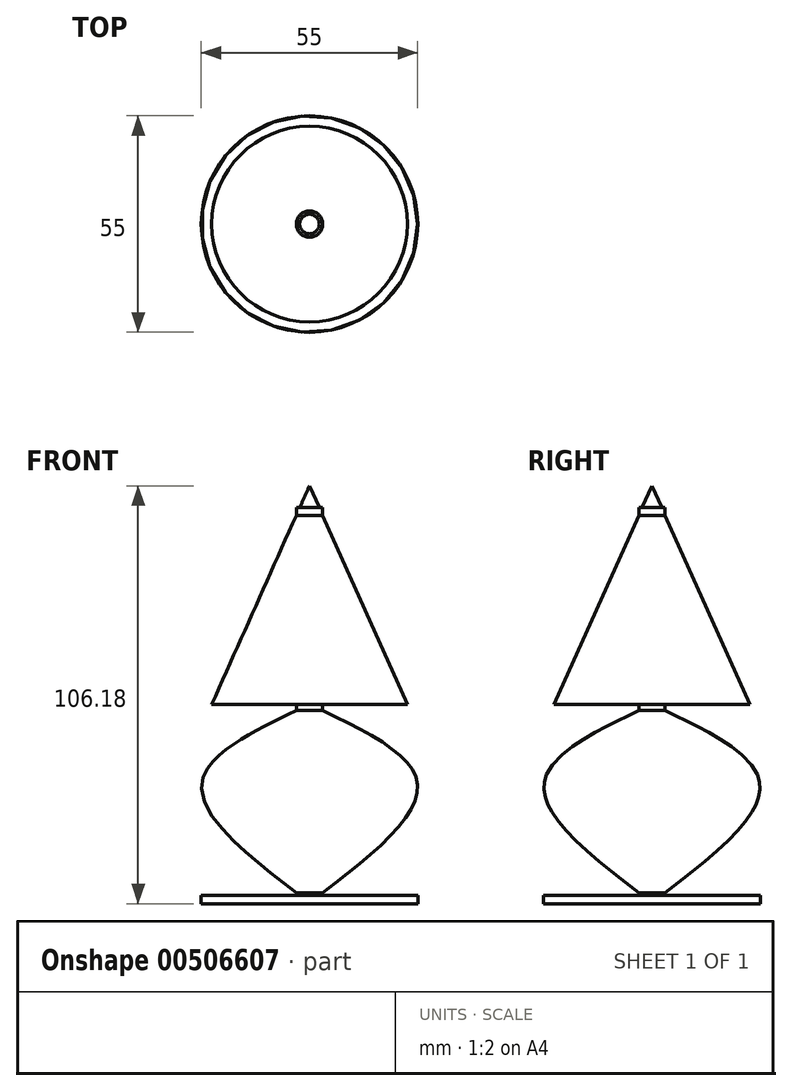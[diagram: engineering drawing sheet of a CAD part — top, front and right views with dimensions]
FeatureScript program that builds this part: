
annotation { "Feature Type Name" : "Feature", "Feature Type Description" : "" }
export const myFeature = defineFeature(function(context is Context, id is Id, definition is map)
    precondition{}
    {
        {
            var Q0;
            Q0=qCreatedBy(makeId("Top.planeOp"),FACE);
            var sketch = newSketch(context, id + "F0", { "sketchPlane" : qUnion([Q0])});
            skCircle(sketch, "E0", {"center": v(0, 0) * mm, "radius": 3.35 * mm});
            skSolve(sketch);
        }
        {
            var Q0;
            Q0=qCreatedBy(makeId("Top.planeOp"),FACE);
            var sketch = newSketch(context, id + "F1", { "sketchPlane" : qUnion([Q0])});
            skSolve(sketch);
        }
        {
            var Q0;
            Q0 = qSketchRegion(id + "F1", true);
            var Q1;
            Q1=makeQuery(id+"F0.imprint","IMPRINT",FACE,{"disambiguationData":[TD([[makeQuery(id+"F0.imprint","IMPRINT",EDGE,{"derivedFrom":sQuery(id+"F0.wireOp",EDGE,"E0")}),1.0]])]});
            extrude(context, id + "F2", {"entities" : qUnion([Q0, Q1]), "endBound" : BoundingType.SYMMETRIC, "depth" : 100 * mm});
        }
        {
            var Q0;
            Q0=qCreatedBy(makeId("Right.planeOp"),FACE);
            var sketch = newSketch(context, id + "F3", { "sketchPlane" : qUnion([Q0])});
            skLineSegment(sketch, "E1", {"start": v(0, 55.57) * mm, "end": v(0, 0) * mm});
            skLineSegment(sketch, "E2", {"start": v(0, 0) * mm, "end": v(-24.85, 0) * mm});
            skLineSegment(sketch, "E3", {"start": v(-24.85, 0) * mm, "end": v(0, 55.57) * mm});
            skSolve(sketch);
        }
        {
            var Q0;
            Q0=makeQuery(id+"F3.imprint","IMPRINT",FACE,{"disambiguationData":[TD([[makeQuery(id+"F3.imprint","IMPRINT",EDGE,{"derivedFrom":sQuery(id+"F3.wireOp",EDGE,"E1")}),-1.0]])]});
            var Q1;
            Q1=sQuery(id+"F3.wireOp",EDGE,"E1");
            revolve(context, id + "F4", {"operationType" : NewBodyOperationType.ADD, "entities" : qUnion([Q0]), "axis" : qUnion([Q1]), "revolveType" : RevolveType.FULL});
        }
        {
            var Q0;
            Q0=qCreatedBy(makeId("Right.planeOp"),FACE);
            var sketch = newSketch(context, id + "F5", { "sketchPlane" : qUnion([Q0])});
            skFitSpline(sketch, "E4", {"points": [v(0, 0) * mm, v(-27.44, -20.31) * mm, v(0, -50.37) * mm], "startDerivative": vector(-83.7, -38.89) * mm, "endDerivative": vector(81.29, -61.53) * mm});
            skLineSegment(sketch, "E5", {"start": v(0, 0) * mm, "end": v(0, -50.37) * mm});
            skSolve(sketch);
        }
        {
            var Q0;
            Q0=makeQuery(id+"F5.imprint","IMPRINT",FACE,{"disambiguationData":[TD([[makeQuery(id+"F5.imprint","IMPRINT",EDGE,{"derivedFrom":sQuery(id+"F5.wireOp",EDGE,"E4")}),1.0]])]});
            var Q1;
            Q1=sQuery(id+"F5.wireOp",EDGE,"E5");
            revolve(context, id + "F6", {"operationType" : NewBodyOperationType.ADD, "entities" : qUnion([Q0]), "axis" : qUnion([Q1]), "revolveType" : RevolveType.FULL});
        }
        {
            var Q0;
            Q0=qCreatedBy(makeId("Right.planeOp"),FACE);
            var sketch = newSketch(context, id + "F7", { "sketchPlane" : qUnion([Q0])});
            skLineSegment(sketch, "E6", {"start": v(0, -48.5) * mm, "end": v(27.5, -48.5) * mm});
            skLineSegment(sketch, "E7", {"start": v(0, -50.6) * mm, "end": v(27.5, -50.6) * mm});
            skLineSegment(sketch, "E8", {"start": v(27.5, -50.6) * mm, "end": v(27.5, -48.5) * mm});
            skLineSegment(sketch, "E9", {"start": v(0, -50.6) * mm, "end": v(0, -48.5) * mm});
            skSolve(sketch);
        }
        {
            var Q0;
            Q0=makeQuery(id+"F7.imprint","IMPRINT",FACE,{"disambiguationData":[TD([[makeQuery(id+"F7.imprint","IMPRINT",EDGE,{"derivedFrom":sQuery(id+"F7.wireOp",EDGE,"E6")}),-1.0]])]});
            var Q1;
            Q1=sQuery(id+"F7.wireOp",EDGE,"E9");
            revolve(context, id + "F8", {"operationType" : NewBodyOperationType.ADD, "entities" : qUnion([Q0]), "axis" : qUnion([Q1]), "revolveType" : RevolveType.FULL});
        }
    });
